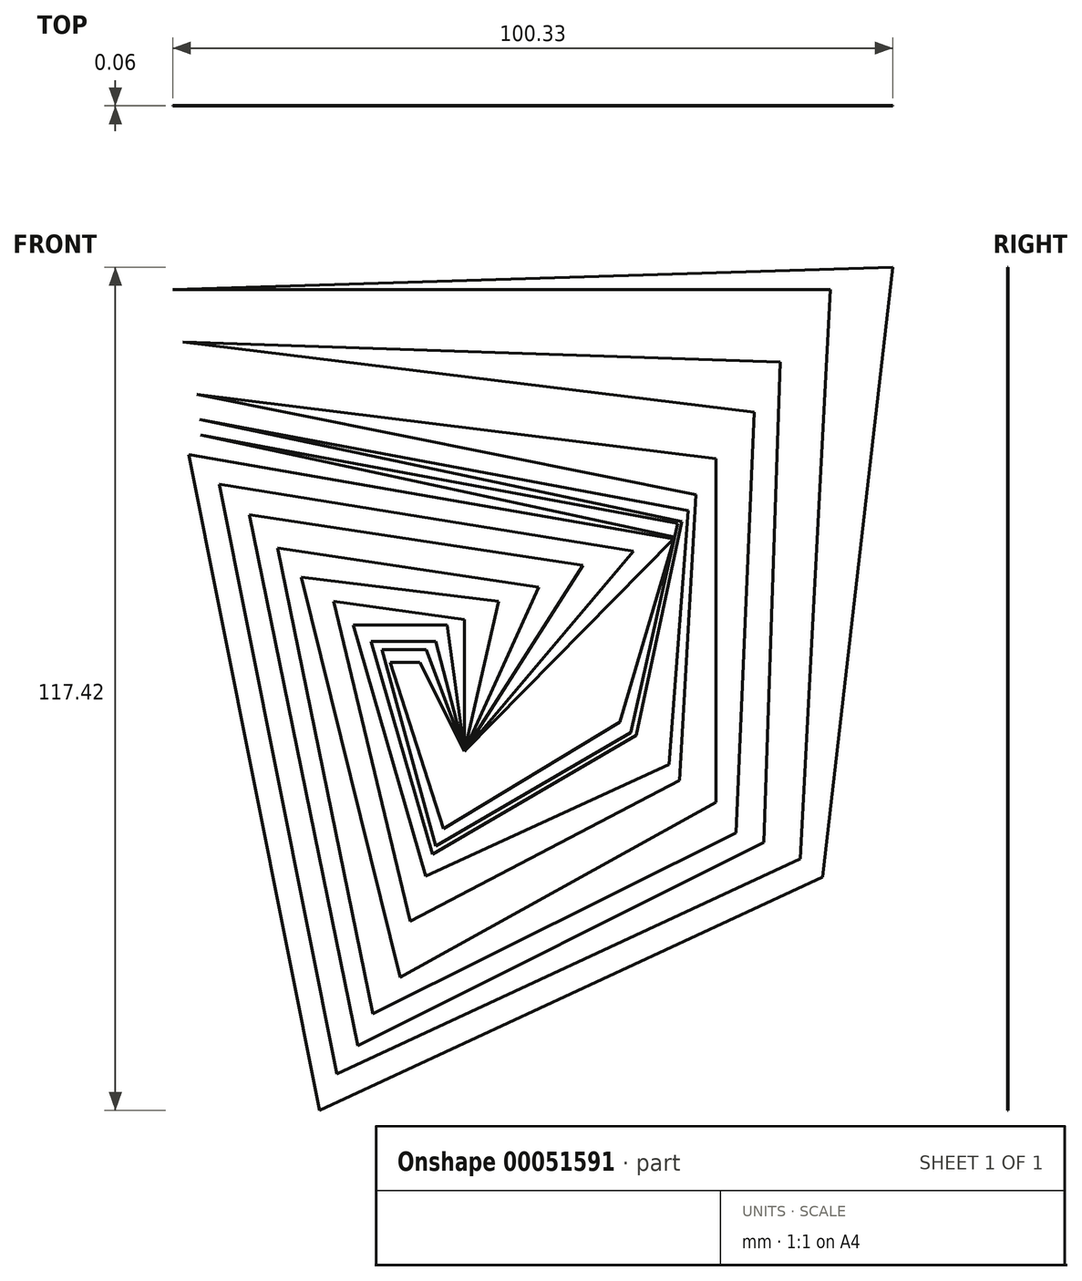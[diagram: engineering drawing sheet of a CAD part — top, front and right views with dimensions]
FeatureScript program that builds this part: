
annotation { "Feature Type Name" : "Feature", "Feature Type Description" : "" }
export const myFeature = defineFeature(function(context is Context, id is Id, definition is map)
    precondition{}
    {
        {
            var Q0;
            Q0=qCreatedBy(makeId("Front.planeOp"),FACE);
            var sketch = newSketch(context, id + "F0", { "sketchPlane" : qUnion([Q0])});
            skLineSegment(sketch, "E0", {"start": v(0, 0) * mm, "end": v(29.15, 29.57) * mm});
            skLineSegment(sketch, "E1", {"start": v(29.15, 29.57) * mm, "end": v(-38.4, 41.34) * mm});
            skLineSegment(sketch, "E2", {"start": v(-38.4, 41.34) * mm, "end": v(-20.18, -50.02) * mm});
            skLineSegment(sketch, "E3", {"start": v(-20.18, -50.02) * mm, "end": v(49.88, -17.52) * mm});
            skLineSegment(sketch, "E4", {"start": v(49.88, -17.52) * mm, "end": v(59.7, 67.4) * mm});
            skLineSegment(sketch, "E5", {"start": v(59.7, 67.4) * mm, "end": v(-40.64, 64.32) * mm});
            skLineSegment(sketch, "E6", {"start": v(-40.64, 64.32) * mm, "end": v(51, 64.32) * mm});
            skLineSegment(sketch, "E7", {"start": v(51, 64.32) * mm, "end": v(46.8, -15) * mm});
            skLineSegment(sketch, "E8", {"start": v(46.8, -15) * mm, "end": v(-17.8, -44.96) * mm});
            skLineSegment(sketch, "E9", {"start": v(-17.8, -44.96) * mm, "end": v(-34.17, 37.2) * mm});
            skLineSegment(sketch, "E10", {"start": v(-34.17, 37.2) * mm, "end": v(23.54, 27.88) * mm});
            skLineSegment(sketch, "E11", {"start": v(23.54, 27.88) * mm, "end": v(0, 0) * mm});
            skSolve(sketch);
        }
        {
            var Q0;
            Q0=makeQuery(id+"F0.imprint","IMPRINT",FACE,{"disambiguationData":[TD([[makeQuery(id+"F0.imprint","IMPRINT",EDGE,{"derivedFrom":sQuery(id+"F0.wireOp",EDGE,"E0")}),1.0]])]});
            extrude(context, id + "F1", {"entities" : qUnion([Q0]), "depth" : 0.06 * mm});
        }
        {
            var Q0;
            Q0=qCreatedBy(makeId("Front.planeOp"),FACE);
            var sketch = newSketch(context, id + "F2", { "sketchPlane" : qUnion([Q0])});
            skLineSegment(sketch, "E12", {"start": v(-39.23, 57.03) * mm, "end": v(44, 54.23) * mm});
            skLineSegment(sketch, "E13", {"start": v(44, 54.23) * mm, "end": v(41.74, -12.73) * mm});
            skLineSegment(sketch, "E14", {"start": v(41.74, -12.73) * mm, "end": v(-14.85, -41.06) * mm});
            skLineSegment(sketch, "E15", {"start": v(-14.85, -41.06) * mm, "end": v(-29.99, 32.93) * mm});
            skLineSegment(sketch, "E16", {"start": v(-29.99, 32.93) * mm, "end": v(16.53, 25.92) * mm});
            skLineSegment(sketch, "E17", {"start": v(16.53, 25.92) * mm, "end": v(0, 0) * mm});
            skLineSegment(sketch, "E18", {"start": v(0, 0) * mm, "end": v(10.37, 22.84) * mm});
            skLineSegment(sketch, "E19", {"start": v(10.37, 22.84) * mm, "end": v(-26.05, 28.33) * mm});
            skLineSegment(sketch, "E20", {"start": v(-26.05, 28.33) * mm, "end": v(-12.77, -36.61) * mm});
            skLineSegment(sketch, "E21", {"start": v(-12.77, -36.61) * mm, "end": v(37.83, -11.35) * mm});
            skLineSegment(sketch, "E22", {"start": v(37.83, -11.35) * mm, "end": v(40.36, 47.22) * mm});
            skLineSegment(sketch, "E23", {"start": v(40.36, 47.22) * mm, "end": v(-39.23, 57.03) * mm});
            skSolve(sketch);
        }
        {
            var Q0;
            Q0=makeQuery(id+"F2.imprint","IMPRINT",FACE,{"disambiguationData":[TD([[makeQuery(id+"F2.imprint","IMPRINT",EDGE,{"derivedFrom":sQuery(id+"F2.wireOp",EDGE,"E12")}),-1.0]])]});
            extrude(context, id + "F3", {"entities" : qUnion([Q0]), "depth" : 0.06 * mm});
        }
        {
            var Q0;
            Q0=qCreatedBy(makeId("Front.planeOp"),FACE);
            var sketch = newSketch(context, id + "F4", { "sketchPlane" : qUnion([Q0])});
            skLineSegment(sketch, "E24", {"start": v(-37.27, 49.74) * mm, "end": v(35.03, 40.78) * mm});
            skLineSegment(sketch, "E25", {"start": v(35.03, 40.78) * mm, "end": v(35.03, -7.15) * mm});
            skLineSegment(sketch, "E26", {"start": v(35.03, -7.15) * mm, "end": v(-8.97, -31.53) * mm});
            skLineSegment(sketch, "E27", {"start": v(-8.97, -31.53) * mm, "end": v(-22.7, 24.24) * mm});
            skLineSegment(sketch, "E28", {"start": v(-22.7, 24.24) * mm, "end": v(4.76, 20.88) * mm});
            skLineSegment(sketch, "E29", {"start": v(4.76, 20.88) * mm, "end": v(0, 0) * mm});
            skLineSegment(sketch, "E30", {"start": v(0, 0) * mm, "end": v(0, 18.36) * mm});
            skLineSegment(sketch, "E31", {"start": v(0, 18.36) * mm, "end": v(-18.22, 20.88) * mm});
            skLineSegment(sketch, "E32", {"start": v(-18.22, 20.88) * mm, "end": v(-7.57, -23.68) * mm});
            skLineSegment(sketch, "E33", {"start": v(-7.57, -23.68) * mm, "end": v(29.99, -4.06) * mm});
            skLineSegment(sketch, "E34", {"start": v(29.99, -4.06) * mm, "end": v(32.23, 35.73) * mm});
            skLineSegment(sketch, "E35", {"start": v(32.23, 35.73) * mm, "end": v(-37.27, 49.74) * mm});
            skSolve(sketch);
        }
        {
            var Q0;
            Q0=makeQuery(id+"F4.imprint","IMPRINT",FACE,{"disambiguationData":[TD([[makeQuery(id+"F4.imprint","IMPRINT",EDGE,{"derivedFrom":sQuery(id+"F4.wireOp",EDGE,"E24")}),-1.0]])]});
            extrude(context, id + "F5", {"entities" : qUnion([Q0]), "depth" : 0.06 * mm});
        }
        {
            var Q0;
            Q0=qCreatedBy(makeId("Front.planeOp"),FACE);
            var sketch = newSketch(context, id + "F6", { "sketchPlane" : qUnion([Q0])});
            skLineSegment(sketch, "E36", {"start": v(-36.88, 46.24) * mm, "end": v(31.16, 33.51) * mm});
            skLineSegment(sketch, "E37", {"start": v(31.16, 33.51) * mm, "end": v(28.5, -1.83) * mm});
            skLineSegment(sketch, "E38", {"start": v(28.5, -1.83) * mm, "end": v(-5.42, -17.38) * mm});
            skLineSegment(sketch, "E39", {"start": v(-5.42, -17.38) * mm, "end": v(-15.5, 17.6) * mm});
            skLineSegment(sketch, "E40", {"start": v(-15.5, 17.6) * mm, "end": v(-2.42, 17.6) * mm});
            skLineSegment(sketch, "E41", {"start": v(-2.42, 17.6) * mm, "end": v(0, 0) * mm});
            skLineSegment(sketch, "E42", {"start": v(0, 0) * mm, "end": v(-4, 15.31) * mm});
            skLineSegment(sketch, "E43", {"start": v(-4, 15.31) * mm, "end": v(-13.02, 15.31) * mm});
            skLineSegment(sketch, "E44", {"start": v(-13.02, 15.31) * mm, "end": v(-4.48, -14.36) * mm});
            skLineSegment(sketch, "E45", {"start": v(-4.48, -14.36) * mm, "end": v(23.91, 2.24) * mm});
            skLineSegment(sketch, "E46", {"start": v(23.91, 2.24) * mm, "end": v(30.3, 32) * mm});
            skLineSegment(sketch, "E47", {"start": v(30.3, 32) * mm, "end": v(-36.88, 46.24) * mm});
            skSolve(sketch);
        }
        {
            var Q0;
            Q0=makeQuery(id+"F6.imprint","IMPRINT",FACE,{"disambiguationData":[TD([[makeQuery(id+"F6.imprint","IMPRINT",EDGE,{"derivedFrom":sQuery(id+"F6.wireOp",EDGE,"E36")}),-1.0]])]});
            extrude(context, id + "F7", {"entities" : qUnion([Q0]), "depth" : 0.06 * mm});
        }
        {
            var Q0;
            Q0=qCreatedBy(makeId("Front.planeOp"),FACE);
            var sketch = newSketch(context, id + "F8", { "sketchPlane" : qUnion([Q0])});
            skLineSegment(sketch, "E48", {"start": v(-36.8, 44.1) * mm, "end": v(29.73, 31.72) * mm});
            skLineSegment(sketch, "E49", {"start": v(29.73, 31.72) * mm, "end": v(23.2, 2.6) * mm});
            skLineSegment(sketch, "E50", {"start": v(23.2, 2.6) * mm, "end": v(-4, -13.23) * mm});
            skLineSegment(sketch, "E51", {"start": v(-4, -13.23) * mm, "end": v(-11.5, 14.15) * mm});
            skLineSegment(sketch, "E52", {"start": v(-11.5, 14.15) * mm, "end": v(-5.32, 14.15) * mm});
            skLineSegment(sketch, "E53", {"start": v(-5.32, 14.15) * mm, "end": v(0, 0) * mm});
            skLineSegment(sketch, "E54", {"start": v(0, 0) * mm, "end": v(-6.25, 12.37) * mm});
            skLineSegment(sketch, "E55", {"start": v(-6.25, 12.37) * mm, "end": v(-10.38, 12.37) * mm});
            skLineSegment(sketch, "E56", {"start": v(-10.38, 12.37) * mm, "end": v(-2.92, -10.81) * mm});
            skLineSegment(sketch, "E57", {"start": v(-2.92, -10.81) * mm, "end": v(21.67, 4.03) * mm});
            skLineSegment(sketch, "E58", {"start": v(21.67, 4.03) * mm, "end": v(29.25, 29.82) * mm});
            skLineSegment(sketch, "E59", {"start": v(29.25, 29.82) * mm, "end": v(-36.8, 44.1) * mm});
            skSolve(sketch);
        }
        {
            var Q0;
            Q0=makeQuery(id+"F8.imprint","IMPRINT",FACE,{"disambiguationData":[TD([[makeQuery(id+"F8.imprint","IMPRINT",EDGE,{"derivedFrom":sQuery(id+"F8.wireOp",EDGE,"E48")}),-1.0]])]});
            extrude(context, id + "F9", {"entities" : qUnion([Q0]), "depth" : 0.06 * mm});
        }
    });
